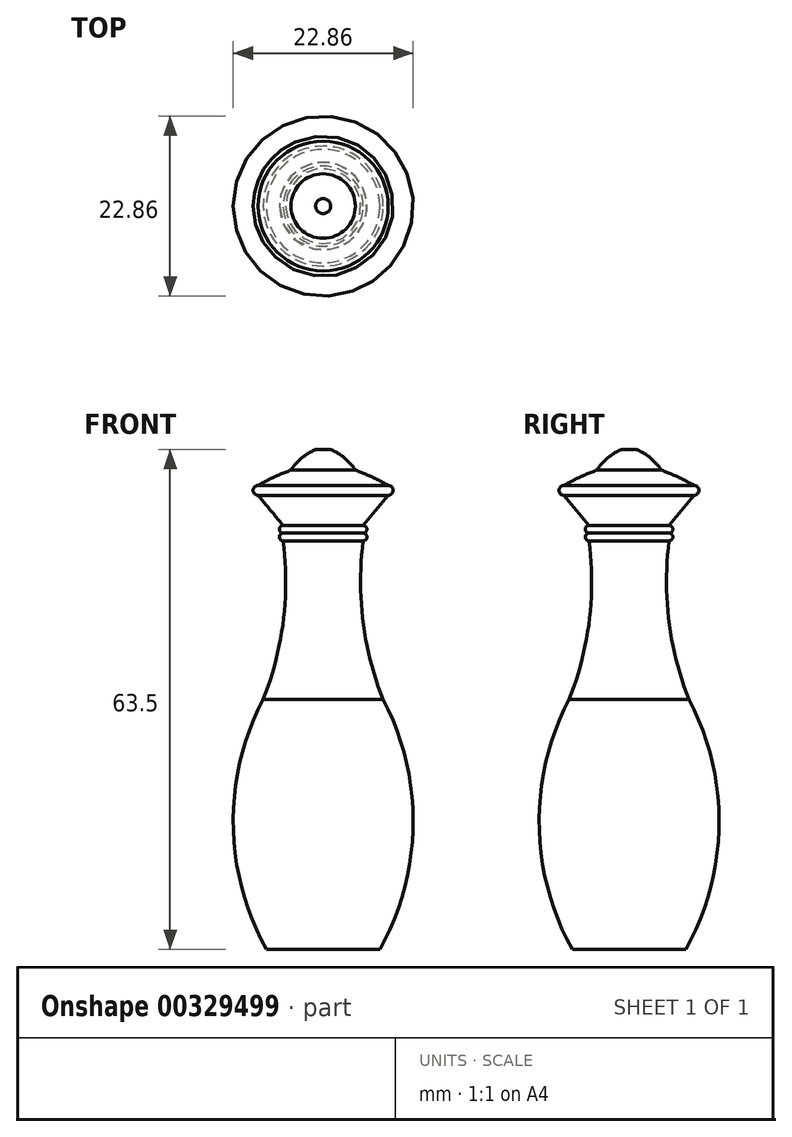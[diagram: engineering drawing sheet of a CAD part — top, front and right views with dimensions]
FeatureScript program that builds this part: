
annotation { "Feature Type Name" : "Feature", "Feature Type Description" : "" }
export const myFeature = defineFeature(function(context is Context, id is Id, definition is map)
    precondition{}
    {
        {
            var Q0;
            Q0=qCreatedBy(makeId("Front.planeOp"),FACE);
            var sketch = newSketch(context, id + "F0", { "sketchPlane" : qUnion([Q0])});
            skLineSegment(sketch, "E0", {"start": v(0, -63.5) * mm, "end": v(7.2, -63.5) * mm});
            skLineSegment(sketch, "E1.MirrorCS", {"start": v(0, -63.5) * mm, "end": v(0, 0) * mm});
            skArc(sketch, "E2.MirrorCS", {"start": v(7.62, -31.75) * mm, "mid": v(11.43, -47.68) * mm, "end": v(7.2, -63.5) * mm});
            skArc(sketch, "E3", {"start": v(5.08, -11.6) * mm, "mid": v(5.07, -21.83) * mm, "end": v(7.62, -31.75) * mm});
            skLineSegment(sketch, "E4", {"start": v(0, 0) * mm, "end": v(0.95, 0) * mm});
            skArc(sketch, "E5", {"start": v(8.26, -4.55) * mm, "mid": v(6.22, -3.5) * mm, "end": v(4.1, -2.62) * mm});
            skLineSegment(sketch, "E6", {"start": v(8.26, -5.82) * mm, "end": v(0, -5.82) * mm});
            skLineSegment(sketch, "E7", {"start": v(8.26, -4.55) * mm, "end": v(0, -4.55) * mm});
            skLineSegment(sketch, "E8", {"start": v(5.08, -11.6) * mm, "end": v(0, -11.6) * mm});
            skArc(sketch, "E9", {"start": v(4.1, -2.62) * mm, "mid": v(2.72, -1.07) * mm, "end": v(0.95, 0) * mm});
            skLineSegment(sketch, "E10", {"start": v(5.08, -10.62) * mm, "end": v(0, -10.62) * mm});
            skArc(sketch, "E11", {"start": v(8.26, -5.82) * mm, "mid": v(8.9, -5.18) * mm, "end": v(8.26, -4.55) * mm});
            skArc(sketch, "E12", {"start": v(5.08, -11.6) * mm, "mid": v(5.57, -11.1) * mm, "end": v(5.08, -10.62) * mm});
            skLineSegment(sketch, "E13", {"start": v(0, -9.66) * mm, "end": v(5.08, -9.66) * mm});
            skLineSegment(sketch, "E14", {"start": v(5.08, -9.66) * mm, "end": v(8.26, -5.82) * mm});
            skArc(sketch, "E15", {"start": v(5.08, -10.62) * mm, "mid": v(5.56, -10.14) * mm, "end": v(5.08, -9.66) * mm});
            skSolve(sketch);
        }
        {
            var Q0;
            Q0 = qSketchRegion(id + "F0", true);
            var Q1;
            Q1=sQuery(id+"F0.wireOp",EDGE,"E1.MirrorCS");
            revolve(context, id + "F1", {"entities" : qUnion([Q0]), "axis" : qUnion([Q1]), "revolveType" : RevolveType.FULL});
        }
    });
